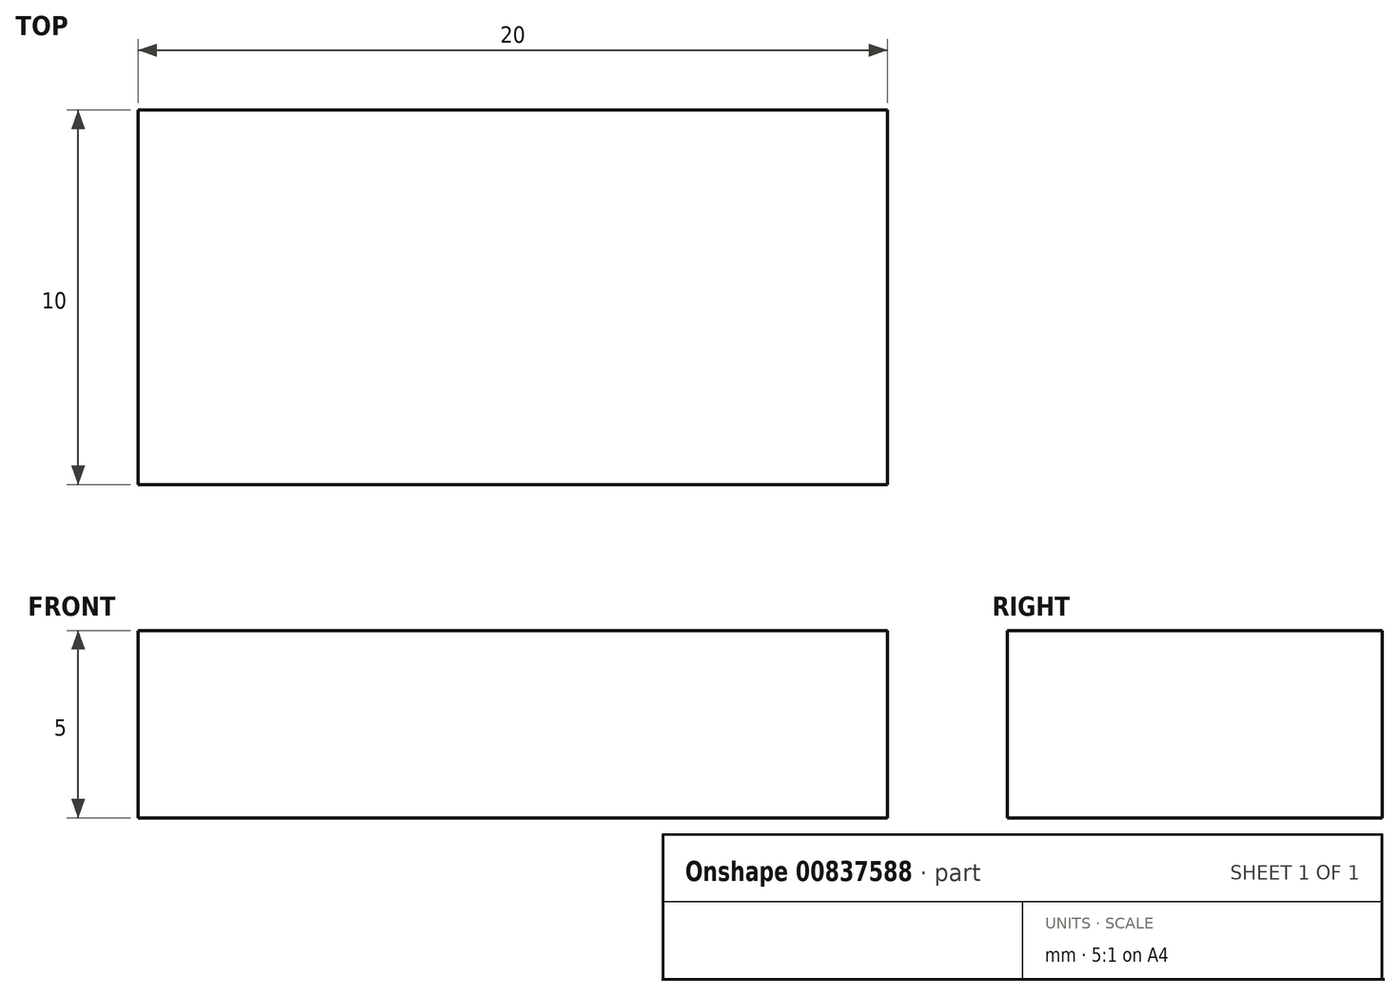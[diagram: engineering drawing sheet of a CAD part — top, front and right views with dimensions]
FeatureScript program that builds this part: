
annotation { "Feature Type Name" : "Feature", "Feature Type Description" : "" }
export const myFeature = defineFeature(function(context is Context, id is Id, definition is map)
    precondition{}
    {
        {
            var Q0;
            Q0=qCreatedBy(makeId("Top.planeOp"),FACE);
            var sketch = newSketch(context, id + "F0", { "sketchPlane" : qUnion([Q0])});
            skLineSegment(sketch, "E0.bottom", {"start": v(23.66, -9.53) * mm, "end": v(43.66, -9.53) * mm});
            skLineSegment(sketch, "E0.top", {"start": v(23.66, -19.53) * mm, "end": v(43.66, -19.53) * mm});
            skLineSegment(sketch, "E0.left", {"start": v(23.66, -9.53) * mm, "end": v(23.66, -19.53) * mm});
            skLineSegment(sketch, "E0.right", {"start": v(43.66, -9.53) * mm, "end": v(43.66, -19.53) * mm});
            skSolve(sketch);
        }
        {
            var Q0;
            Q0 = qSketchRegion(id + "F0", true);
            extrude(context, id + "F1", {"entities" : qUnion([Q0]), "depth" : 5 * mm, "offsetDistance" : 25 * mm});
        }
    });
